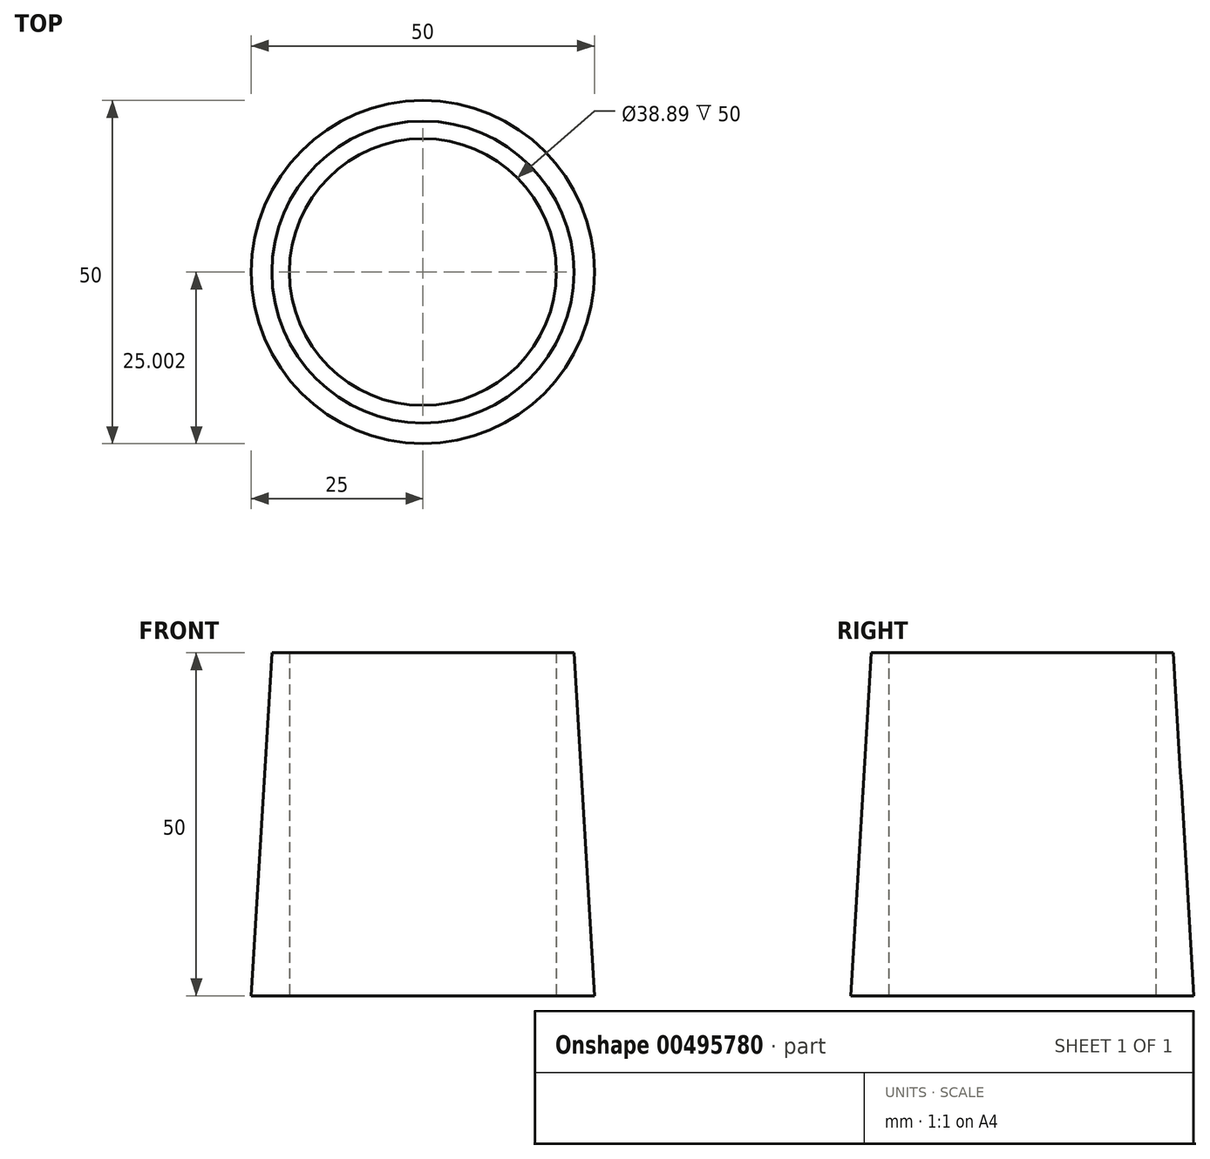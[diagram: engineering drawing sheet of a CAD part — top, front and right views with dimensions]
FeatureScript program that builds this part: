
annotation { "Feature Type Name" : "Feature", "Feature Type Description" : "" }
export const myFeature = defineFeature(function(context is Context, id is Id, definition is map)
    precondition{}
    {
        {
            var Q0;
            Q0=qCreatedBy(makeId("Right.planeOp"),FACE);
            var sketch = newSketch(context, id + "F0", { "sketchPlane" : qUnion([Q0])});
            skLineSegment(sketch, "E0", {"start": v(-53.98, -32.13) * mm, "end": v(-28.98, -32.13) * mm});
            skLineSegment(sketch, "E1", {"start": v(-28.98, -32.13) * mm, "end": v(-28.98, 17.87) * mm});
            skLineSegment(sketch, "E2", {"start": v(-28.98, 17.87) * mm, "end": v(-50.98, 17.87) * mm});
            skLineSegment(sketch, "E3", {"start": v(-50.98, 17.87) * mm, "end": v(-53.98, -32.13) * mm});
            skSolve(sketch);
        }
        {
            var Q0;
            Q0=makeQuery(id+"F0.imprint","IMPRINT",FACE,{"disambiguationData":[TD([[makeQuery(id+"F0.imprint","IMPRINT",EDGE,{"derivedFrom":sQuery(id+"F0.wireOp",EDGE,"E0")}),1.0]])]});
            var Q1;
            Q1=sQuery(id+"F0.wireOp",EDGE,"E1");
            revolve(context, id + "F1", {"entities" : qUnion([Q0]), "axis" : qUnion([Q1]), "revolveType" : RevolveType.FULL});
        }
        {
            var Q0;
            Q0=makeQuery(id+"F1.opRevolve","SWEPT_FACE",FACE,{"disambiguationData":[OSD([sQuery(id+"F0.wireOp",EDGE,"E0")])]});
            var sketch = newSketch(context, id + "F2", { "sketchPlane" : qUnion([Q0])});
            skPoint(sketch, "E4", {"position": v(0, 28.98) * mm});
            skSolve(sketch);
        }
        {
            var Q0;
            Q0=sQuery(id+"F2.wireOp",VERTEX,"E4");
            var Q1;
            Q1=makeQuery(id+"F1.opRevolve","SWEPT_BODY",BODY,{"disambiguationData":[OSD([sQuery(id+"F0.wireOp",EDGE,"E0"),sQuery(id+"F0.wireOp",EDGE,"E1"),sQuery(id+"F0.wireOp",EDGE,"E2"),sQuery(id+"F0.wireOp",EDGE,"E3")])]});
            hole(context, id + "F3", {"style" : HoleStyle.SIMPLE, "endStyle" : HoleEndStyle.BLIND, "standardTappedOrClearance" : lookupTablePath({ "standard" : "ANSI", "fit" : "Normal (ASME)", "size" : "1 1/2", "type" : "Clearance" }), "standardBlindInLast" : lookupTablePath({ "fit" : "Free", "standard" : "ANSI", "size" : "1 1/2", "type" : "Clearance" }), "holeDiameter" : 38.9 * mm, "majorDiameter" : 5 * mm, "holeDepth" : 100 * mm, "isTappedThrough" : true, "tappedDepth" : 12 * mm, "tapClearance" : 3, "locations" : qUnion([Q0]), "scope" : qUnion([Q1])});
        }
    });
